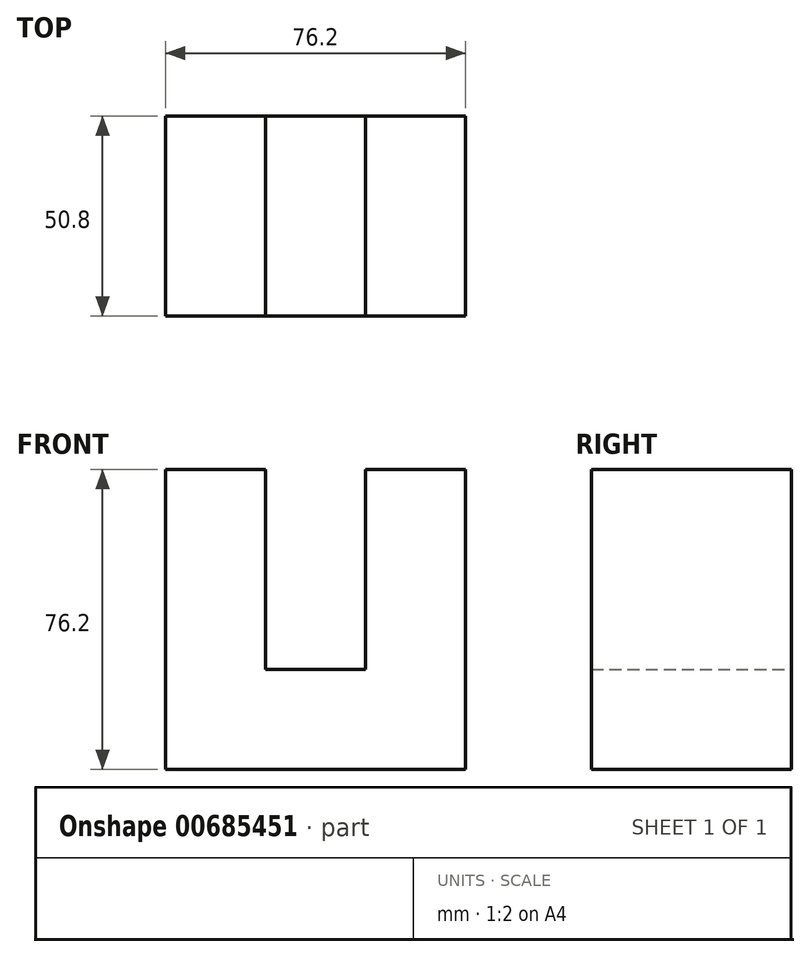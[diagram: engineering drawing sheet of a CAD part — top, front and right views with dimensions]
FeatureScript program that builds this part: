
annotation { "Feature Type Name" : "Feature", "Feature Type Description" : "" }
export const myFeature = defineFeature(function(context is Context, id is Id, definition is map)
    precondition{}
    {
        {
            var Q0;
            Q0=qCreatedBy(makeId("Front.planeOp"),FACE);
            var sketch = newSketch(context, id + "F0", { "sketchPlane" : qUnion([Q0])});
            skLineSegment(sketch, "E0", {"start": v(0, 0) * mm, "end": v(-76.2, 0) * mm});
            skLineSegment(sketch, "E1", {"start": v(-76.2, 0) * mm, "end": v(-76.2, 76.2) * mm});
            skLineSegment(sketch, "E2", {"start": v(-76.2, 76.2) * mm, "end": v(-50.8, 76.2) * mm});
            skLineSegment(sketch, "E3", {"start": v(0, 0) * mm, "end": v(0, 76.2) * mm});
            skLineSegment(sketch, "E4", {"start": v(0, 76.2) * mm, "end": v(-25.4, 76.2) * mm});
            skLineSegment(sketch, "E5", {"start": v(-25.4, 76.2) * mm, "end": v(-25.4, 25.4) * mm});
            skLineSegment(sketch, "E6", {"start": v(-50.8, 76.2) * mm, "end": v(-50.8, 25.4) * mm});
            skLineSegment(sketch, "E7", {"start": v(-50.8, 25.4) * mm, "end": v(-25.4, 25.4) * mm});
            skSolve(sketch);
        }
        {
            var Q0;
            Q0 = qSketchRegion(id + "F0", true);
            extrude(context, id + "F1", {"entities" : qUnion([Q0]), "depth" : 50.8 * mm, "offsetDistance" : 25.4 * mm});
        }
    });
